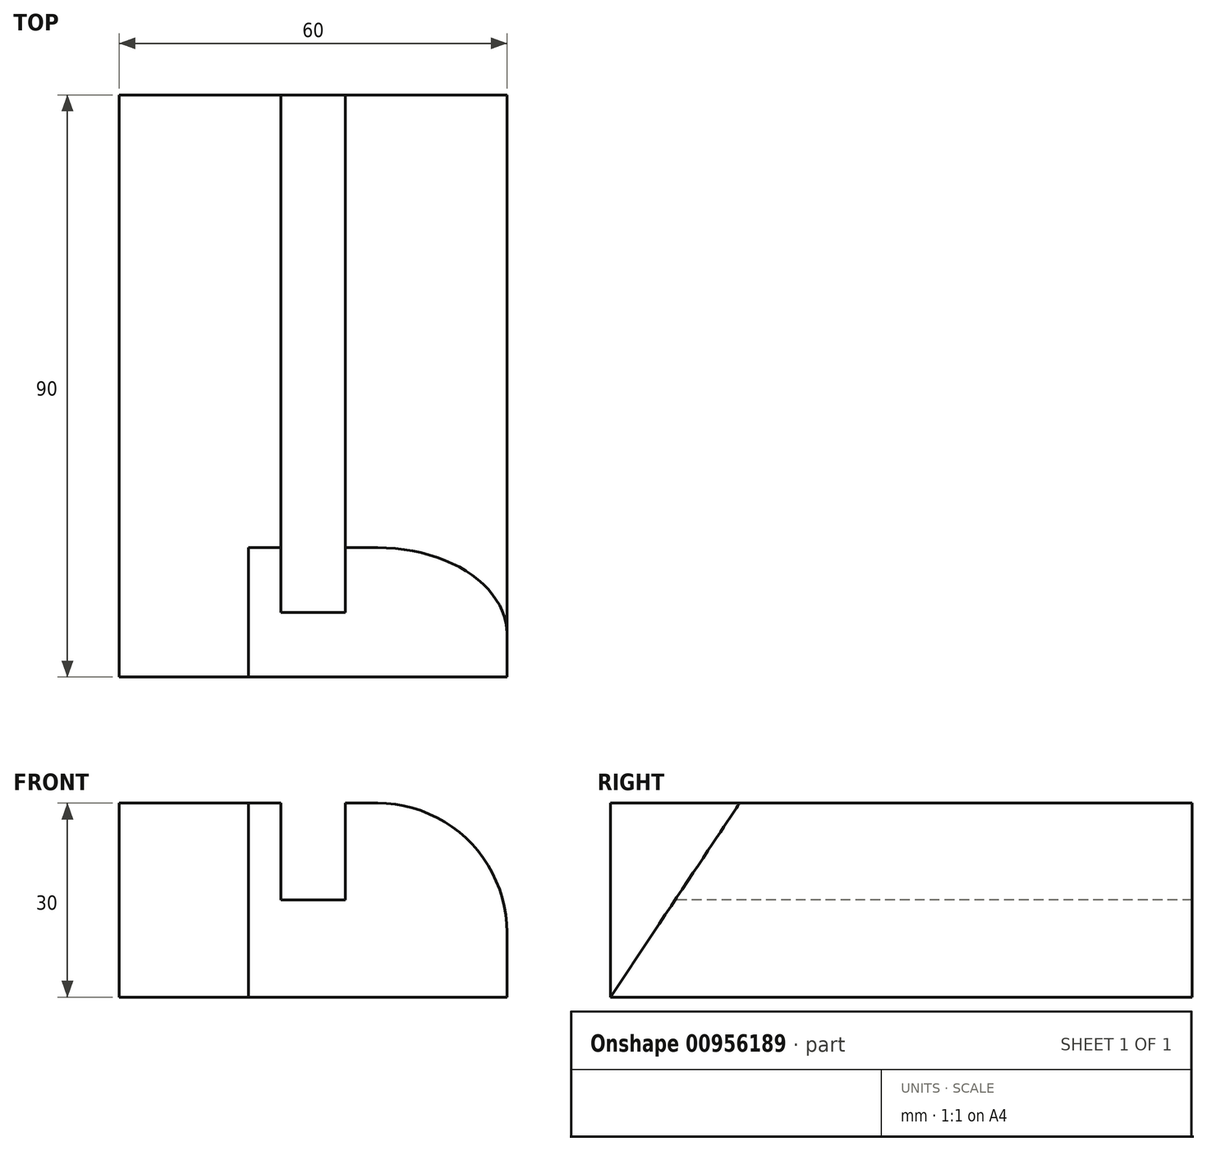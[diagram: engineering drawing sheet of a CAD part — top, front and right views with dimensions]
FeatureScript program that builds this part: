
annotation { "Feature Type Name" : "Feature", "Feature Type Description" : "" }
export const myFeature = defineFeature(function(context is Context, id is Id, definition is map)
    precondition{}
    {
        {
            var Q0;
            Q0=qCreatedBy(makeId("Top.planeOp"),FACE);
            var sketch = newSketch(context, id + "F0", { "sketchPlane" : qUnion([Q0])});
            skLineSegment(sketch, "E0.bottom", {"start": v(0, 0) * mm, "end": v(60, 0) * mm});
            skLineSegment(sketch, "E0.top", {"start": v(0, 90) * mm, "end": v(60, 90) * mm});
            skLineSegment(sketch, "E0.left", {"start": v(0, 0) * mm, "end": v(0, 90) * mm});
            skLineSegment(sketch, "E0.right", {"start": v(60, 0) * mm, "end": v(60, 90) * mm});
            skSolve(sketch);
        }
        {
            var Q0;
            Q0 = qSketchRegion(id + "F0", true);
            extrude(context, id + "F1", {"entities" : qUnion([Q0]), "depth" : 30 * mm, "offsetDistance" : 25 * mm});
        }
        {
            var Q0;
            Q0=makeQuery(id+"F1.opExtrude","CAP_EDGE",EDGE,{"disambiguationData":[OSD([sQuery(id+"F0.wireOp",EDGE,"E0.right")])],"isStart":false});
            fillet(context, id + "F2", {"entities" : qUnion([Q0]), "radius" : 20 * mm, "tangentPropagation" : true, "allowEdgeOverflow" : false});
        }
        {
            var Q0;
            Q0=makeQuery(id+"F1.opExtrude","SWEPT_FACE",FACE,{"disambiguationData":[OSD([sQuery(id+"F0.wireOp",EDGE,"E0.bottom")])]});
            var sketch = newSketch(context, id + "F3", { "sketchPlane" : qUnion([Q0])});
            skLineSegment(sketch, "E1.bottom", {"start": v(25, 30) * mm, "end": v(35, 30) * mm});
            skLineSegment(sketch, "E1.top", {"start": v(25, 15) * mm, "end": v(35, 15) * mm});
            skLineSegment(sketch, "E1.left", {"start": v(25, 30) * mm, "end": v(25, 15) * mm});
            skLineSegment(sketch, "E1.right", {"start": v(35, 30) * mm, "end": v(35, 15) * mm});
            skSolve(sketch);
        }
        {
            var Q0;
            Q0 = qSketchRegion(id + "F3", true);
            extrude(context, id + "F4", {"entities" : qUnion([Q0]), "operationType" : NewBodyOperationType.REMOVE, "endBound" : BoundingType.THROUGH_ALL, "oppositeDirection" : true, "depth" : 25 * mm, "offsetDistance" : 25 * mm});
        }
        {
            var Q0;
            Q0=makeQuery(id+"F1.opExtrude","SWEPT_FACE",FACE,{"disambiguationData":[OSD([sQuery(id+"F0.wireOp",EDGE,"E0.left")])]});
            cPlane(context, id + "F5", {"entities" : qUnion([Q0]), "cplaneType" : CPlaneType.OFFSET, "offset" : 20 * mm, "oppositeDirection" : true, "width" : 150 * mm, "height" : 150 * mm});
        }
        {
            var Q0;
            Q0=qCreatedBy(id+"F5.planeOp",FACE);
            var sketch = newSketch(context, id + "F6", { "sketchPlane" : qUnion([Q0])});
            skLineSegment(sketch, "E2", {"start": v(0, 0) * mm, "end": v(0, 30) * mm});
            skLineSegment(sketch, "E3", {"start": v(0, 30) * mm, "end": v(-20, 30) * mm});
            skLineSegment(sketch, "E4", {"start": v(-20, 30) * mm, "end": v(0, 0) * mm});
            skSolve(sketch);
        }
        {
            var Q0;
            Q0 = qSketchRegion(id + "F6", true);
            extrude(context, id + "F7", {"entities" : qUnion([Q0]), "operationType" : NewBodyOperationType.REMOVE, "endBound" : BoundingType.THROUGH_ALL, "oppositeDirection" : true, "depth" : 25 * mm, "offsetDistance" : 25 * mm});
        }
    });
